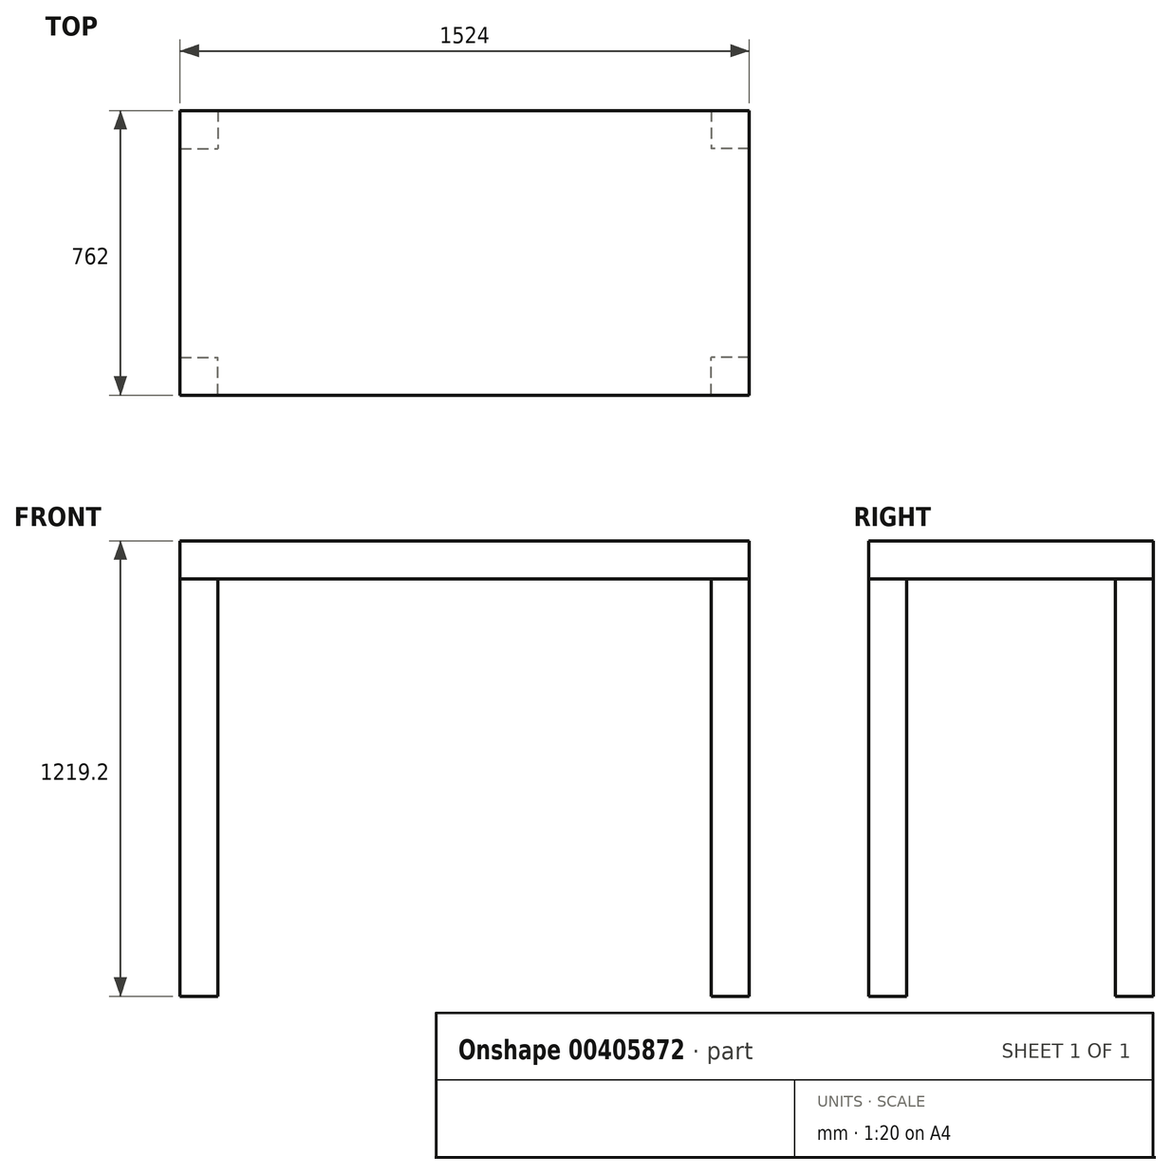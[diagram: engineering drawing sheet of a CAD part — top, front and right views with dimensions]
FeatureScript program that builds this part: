
annotation { "Feature Type Name" : "Feature", "Feature Type Description" : "" }
export const myFeature = defineFeature(function(context is Context, id is Id, definition is map)
    precondition{}
    {
        {
            assignVariable(context, id + "F0", {"name" : "TopThickness", "anyValue" : 101.6 * mm});
        }
        {
            assignVariable(context, id + "F1", {"name" : "Height", "anyValue" : 1219.2 * mm});
        }
        {
            var Q0;
            Q0=qCreatedBy(makeId("Top.planeOp"),FACE);
            var sketch = newSketch(context, id + "F2", { "sketchPlane" : qUnion([Q0])});
            skLineSegment(sketch, "E0", {"start": v(-762, 0) * mm, "end": v(762, 0) * mm, "construction": true});
            skLineSegment(sketch, "E1", {"start": v(0, 381) * mm, "end": v(0, -381) * mm, "construction": true});
            skLineSegment(sketch, "E2.bottom", {"start": v(-762, 381) * mm, "end": v(762, 381) * mm, "construction": true});
            skLineSegment(sketch, "E2.top", {"start": v(-762, -381) * mm, "end": v(762, -381) * mm, "construction": true});
            skLineSegment(sketch, "E2.left", {"start": v(-762, 381) * mm, "end": v(-762, -381) * mm, "construction": true});
            skLineSegment(sketch, "E2.right", {"start": v(762, 381) * mm, "end": v(762, -381) * mm, "construction": true});
            skSolve(sketch);
        }
        {
            var Q0;
            Q0=qCreatedBy(makeId("Top.planeOp"),FACE);
            cPlane(context, id + "F3", {"entities" : qUnion([Q0]), "cplaneType" : CPlaneType.OFFSET, "offset" : getVariable(context, 'TopThickness'), "width" : 152.4 * mm, "height" : 152.4 * mm});
        }
        {
            var Q0;
            Q0=qCreatedBy(makeId("Top.planeOp"),FACE);
            var sketch = newSketch(context, id + "F4", { "sketchPlane" : qUnion([Q0])});
            skPoint(sketch, "E3.0", {"position": v(-762, 381) * mm});
            skPoint(sketch, "E4.0", {"position": v(762, 381) * mm});
            skPoint(sketch, "E5.0", {"position": v(762, -381) * mm});
            skLineSegment(sketch, "E6.bottom", {"start": v(-762, 381) * mm, "end": v(-660.4, 381) * mm});
            skLineSegment(sketch, "E6.top", {"start": v(-762, 279.4) * mm, "end": v(-660.4, 279.4) * mm});
            skLineSegment(sketch, "E6.left", {"start": v(-762, 381) * mm, "end": v(-762, 279.4) * mm});
            skLineSegment(sketch, "E6.right", {"start": v(-660.4, 381) * mm, "end": v(-660.4, 279.4) * mm});
            skLineSegment(sketch, "E7.bottom", {"start": v(762, 381) * mm, "end": v(660.4, 381) * mm});
            skLineSegment(sketch, "E7.top", {"start": v(762, 279.4) * mm, "end": v(660.4, 279.4) * mm});
            skLineSegment(sketch, "E7.left", {"start": v(762, 381) * mm, "end": v(762, 279.4) * mm});
            skLineSegment(sketch, "E7.right", {"start": v(660.4, 381) * mm, "end": v(660.4, 279.4) * mm});
            skLineSegment(sketch, "E8.bottom", {"start": v(762, -381) * mm, "end": v(660.4, -381) * mm});
            skLineSegment(sketch, "E8.top", {"start": v(762, -279.4) * mm, "end": v(660.4, -279.4) * mm});
            skLineSegment(sketch, "E8.left", {"start": v(762, -381) * mm, "end": v(762, -279.4) * mm});
            skLineSegment(sketch, "E8.right", {"start": v(660.4, -381) * mm, "end": v(660.4, -279.4) * mm});
            skPoint(sketch, "E9.0", {"position": v(-762, -381) * mm});
            skLineSegment(sketch, "E10.bottom", {"start": v(-762, -381) * mm, "end": v(-660.4, -381) * mm});
            skLineSegment(sketch, "E10.top", {"start": v(-762, -279.4) * mm, "end": v(-660.4, -279.4) * mm});
            skLineSegment(sketch, "E10.left", {"start": v(-762, -381) * mm, "end": v(-762, -279.4) * mm});
            skLineSegment(sketch, "E10.right", {"start": v(-660.4, -381) * mm, "end": v(-660.4, -279.4) * mm});
            skSolve(sketch);
        }
        {
            var Q0;
            Q0 = qSketchRegion(id + "F4", true);
            extrude(context, id + "F5", {"entities" : qUnion([Q0]), "oppositeDirection" : true, "depth" : getVariable(context, 'Height') - getVariable(context, 'TopThickness')});
        }
        {
            var Q0;
            Q0=qCreatedBy(id+"F3.planeOp",FACE);
            var sketch = newSketch(context, id + "F6", { "sketchPlane" : qUnion([Q0])});
            skLineSegment(sketch, "E11.bottom", {"start": v(-762, -381) * mm, "end": v(762, -381) * mm});
            skLineSegment(sketch, "E11.top", {"start": v(-762, -330.2) * mm, "end": v(762, -330.2) * mm});
            skLineSegment(sketch, "E11.left", {"start": v(-762, -381) * mm, "end": v(-762, -330.2) * mm});
            skLineSegment(sketch, "E11.right", {"start": v(762, -381) * mm, "end": v(762, -330.2) * mm});
            skPoint(sketch, "E12.0", {"position": v(-762, -381) * mm});
            skLineSegment(sketch, "E13.0.1.0", {"start": v(-762, -279.4) * mm, "end": v(762, -279.4) * mm});
            skLineSegment(sketch, "E13.0.1.2", {"start": v(-762, -330.2) * mm, "end": v(-762, -279.4) * mm});
            skLineSegment(sketch, "E13.0.1.3", {"start": v(762, -330.2) * mm, "end": v(762, -279.4) * mm});
            skLineSegment(sketch, "E13.0.2.0", {"start": v(-762, -228.6) * mm, "end": v(762, -228.6) * mm});
            skLineSegment(sketch, "E13.0.2.1", {"start": v(-762, -279.4) * mm, "end": v(762, -279.4) * mm});
            skLineSegment(sketch, "E13.0.2.2", {"start": v(-762, -279.4) * mm, "end": v(-762, -228.6) * mm});
            skLineSegment(sketch, "E13.0.2.3", {"start": v(762, -279.4) * mm, "end": v(762, -228.6) * mm});
            skLineSegment(sketch, "E13.0.3.0", {"start": v(-762, -177.8) * mm, "end": v(762, -177.8) * mm});
            skLineSegment(sketch, "E13.0.3.1", {"start": v(-762, -228.6) * mm, "end": v(762, -228.6) * mm});
            skLineSegment(sketch, "E13.0.3.2", {"start": v(-762, -228.6) * mm, "end": v(-762, -177.8) * mm});
            skLineSegment(sketch, "E13.0.3.3", {"start": v(762, -228.6) * mm, "end": v(762, -177.8) * mm});
            skLineSegment(sketch, "E13.0.4.0", {"start": v(-762, -127) * mm, "end": v(762, -127) * mm});
            skLineSegment(sketch, "E13.0.4.1", {"start": v(-762, -177.8) * mm, "end": v(762, -177.8) * mm});
            skLineSegment(sketch, "E13.0.4.2", {"start": v(-762, -177.8) * mm, "end": v(-762, -127) * mm});
            skLineSegment(sketch, "E13.0.4.3", {"start": v(762, -177.8) * mm, "end": v(762, -127) * mm});
            skLineSegment(sketch, "E13.0.5.0", {"start": v(-762, -76.2) * mm, "end": v(762, -76.2) * mm});
            skLineSegment(sketch, "E13.0.5.1", {"start": v(-762, -127) * mm, "end": v(762, -127) * mm});
            skLineSegment(sketch, "E13.0.5.2", {"start": v(-762, -127) * mm, "end": v(-762, -76.2) * mm});
            skLineSegment(sketch, "E13.0.5.3", {"start": v(762, -127) * mm, "end": v(762, -76.2) * mm});
            skLineSegment(sketch, "E13.0.6.0", {"start": v(-762, -25.4) * mm, "end": v(762, -25.4) * mm});
            skLineSegment(sketch, "E13.0.6.1", {"start": v(-762, -76.2) * mm, "end": v(762, -76.2) * mm});
            skLineSegment(sketch, "E13.0.6.2", {"start": v(-762, -76.2) * mm, "end": v(-762, -25.4) * mm});
            skLineSegment(sketch, "E13.0.6.3", {"start": v(762, -76.2) * mm, "end": v(762, -25.4) * mm});
            skLineSegment(sketch, "E13.0.7.0", {"start": v(-762, 25.4) * mm, "end": v(762, 25.4) * mm});
            skLineSegment(sketch, "E13.0.7.1", {"start": v(-762, -25.4) * mm, "end": v(762, -25.4) * mm});
            skLineSegment(sketch, "E13.0.7.2", {"start": v(-762, -25.4) * mm, "end": v(-762, 25.4) * mm});
            skLineSegment(sketch, "E13.0.7.3", {"start": v(762, -25.4) * mm, "end": v(762, 25.4) * mm});
            skLineSegment(sketch, "E13.0.8.0", {"start": v(-762, 76.2) * mm, "end": v(762, 76.2) * mm});
            skLineSegment(sketch, "E13.0.8.1", {"start": v(-762, 25.4) * mm, "end": v(762, 25.4) * mm});
            skLineSegment(sketch, "E13.0.8.2", {"start": v(-762, 25.4) * mm, "end": v(-762, 76.2) * mm});
            skLineSegment(sketch, "E13.0.8.3", {"start": v(762, 25.4) * mm, "end": v(762, 76.2) * mm});
            skLineSegment(sketch, "E13.0.9.0", {"start": v(-762, 127) * mm, "end": v(762, 127) * mm});
            skLineSegment(sketch, "E13.0.9.1", {"start": v(-762, 76.2) * mm, "end": v(762, 76.2) * mm});
            skLineSegment(sketch, "E13.0.9.2", {"start": v(-762, 76.2) * mm, "end": v(-762, 127) * mm});
            skLineSegment(sketch, "E13.0.9.3", {"start": v(762, 76.2) * mm, "end": v(762, 127) * mm});
            skLineSegment(sketch, "E13.0.10.0", {"start": v(-762, 177.8) * mm, "end": v(762, 177.8) * mm});
            skLineSegment(sketch, "E13.0.10.1", {"start": v(-762, 127) * mm, "end": v(762, 127) * mm});
            skLineSegment(sketch, "E13.0.10.2", {"start": v(-762, 127) * mm, "end": v(-762, 177.8) * mm});
            skLineSegment(sketch, "E13.0.10.3", {"start": v(762, 127) * mm, "end": v(762, 177.8) * mm});
            skLineSegment(sketch, "E13.0.11.0", {"start": v(-762, 228.6) * mm, "end": v(762, 228.6) * mm});
            skLineSegment(sketch, "E13.0.11.1", {"start": v(-762, 177.8) * mm, "end": v(762, 177.8) * mm});
            skLineSegment(sketch, "E13.0.11.2", {"start": v(-762, 177.8) * mm, "end": v(-762, 228.6) * mm});
            skLineSegment(sketch, "E13.0.11.3", {"start": v(762, 177.8) * mm, "end": v(762, 228.6) * mm});
            skLineSegment(sketch, "E13.0.12.0", {"start": v(-762, 279.4) * mm, "end": v(762, 279.4) * mm});
            skLineSegment(sketch, "E13.0.12.1", {"start": v(-762, 228.6) * mm, "end": v(762, 228.6) * mm});
            skLineSegment(sketch, "E13.0.12.2", {"start": v(-762, 228.6) * mm, "end": v(-762, 279.4) * mm});
            skLineSegment(sketch, "E13.0.12.3", {"start": v(762, 228.6) * mm, "end": v(762, 279.4) * mm});
            skLineSegment(sketch, "E13.0.13.0", {"start": v(-762, 330.2) * mm, "end": v(762, 330.2) * mm});
            skLineSegment(sketch, "E13.0.13.1", {"start": v(-762, 279.4) * mm, "end": v(762, 279.4) * mm});
            skLineSegment(sketch, "E13.0.13.2", {"start": v(-762, 279.4) * mm, "end": v(-762, 330.2) * mm});
            skLineSegment(sketch, "E13.0.13.3", {"start": v(762, 279.4) * mm, "end": v(762, 330.2) * mm});
            skLineSegment(sketch, "E13.0.14.0", {"start": v(-762, 381) * mm, "end": v(762, 381) * mm});
            skLineSegment(sketch, "E13.0.14.1", {"start": v(-762, 330.2) * mm, "end": v(762, 330.2) * mm});
            skLineSegment(sketch, "E13.0.14.2", {"start": v(-762, 330.2) * mm, "end": v(-762, 381) * mm});
            skLineSegment(sketch, "E13.0.14.3", {"start": v(762, 330.2) * mm, "end": v(762, 381) * mm});
            skLineSegment(sketch, "E13.1.1.0", {"start": v(-762, -279.4) * mm, "end": v(762, -279.4) * mm});
            skLineSegment(sketch, "E13.1.1.2", {"start": v(-762, -330.2) * mm, "end": v(-762, -279.4) * mm});
            skLineSegment(sketch, "E13.1.1.3", {"start": v(762, -330.2) * mm, "end": v(762, -279.4) * mm});
            skLineSegment(sketch, "E13.1.2.0", {"start": v(-762, -228.6) * mm, "end": v(762, -228.6) * mm});
            skLineSegment(sketch, "E13.1.2.1", {"start": v(-762, -279.4) * mm, "end": v(762, -279.4) * mm});
            skLineSegment(sketch, "E13.1.2.2", {"start": v(-762, -279.4) * mm, "end": v(-762, -228.6) * mm});
            skLineSegment(sketch, "E13.1.2.3", {"start": v(762, -279.4) * mm, "end": v(762, -228.6) * mm});
            skLineSegment(sketch, "E13.1.3.0", {"start": v(-762, -177.8) * mm, "end": v(762, -177.8) * mm});
            skLineSegment(sketch, "E13.1.3.1", {"start": v(-762, -228.6) * mm, "end": v(762, -228.6) * mm});
            skLineSegment(sketch, "E13.1.3.2", {"start": v(-762, -228.6) * mm, "end": v(-762, -177.8) * mm});
            skLineSegment(sketch, "E13.1.3.3", {"start": v(762, -228.6) * mm, "end": v(762, -177.8) * mm});
            skLineSegment(sketch, "E13.1.4.0", {"start": v(-762, -127) * mm, "end": v(762, -127) * mm});
            skLineSegment(sketch, "E13.1.4.1", {"start": v(-762, -177.8) * mm, "end": v(762, -177.8) * mm});
            skLineSegment(sketch, "E13.1.4.2", {"start": v(-762, -177.8) * mm, "end": v(-762, -127) * mm});
            skLineSegment(sketch, "E13.1.4.3", {"start": v(762, -177.8) * mm, "end": v(762, -127) * mm});
            skLineSegment(sketch, "E13.1.5.0", {"start": v(-762, -76.2) * mm, "end": v(762, -76.2) * mm});
            skLineSegment(sketch, "E13.1.5.1", {"start": v(-762, -127) * mm, "end": v(762, -127) * mm});
            skLineSegment(sketch, "E13.1.5.2", {"start": v(-762, -127) * mm, "end": v(-762, -76.2) * mm});
            skLineSegment(sketch, "E13.1.5.3", {"start": v(762, -127) * mm, "end": v(762, -76.2) * mm});
            skLineSegment(sketch, "E13.1.6.0", {"start": v(-762, -25.4) * mm, "end": v(762, -25.4) * mm});
            skLineSegment(sketch, "E13.1.6.1", {"start": v(-762, -76.2) * mm, "end": v(762, -76.2) * mm});
            skLineSegment(sketch, "E13.1.6.2", {"start": v(-762, -76.2) * mm, "end": v(-762, -25.4) * mm});
            skLineSegment(sketch, "E13.1.6.3", {"start": v(762, -76.2) * mm, "end": v(762, -25.4) * mm});
            skLineSegment(sketch, "E13.1.7.0", {"start": v(-762, 25.4) * mm, "end": v(762, 25.4) * mm});
            skLineSegment(sketch, "E13.1.7.1", {"start": v(-762, -25.4) * mm, "end": v(762, -25.4) * mm});
            skLineSegment(sketch, "E13.1.7.2", {"start": v(-762, -25.4) * mm, "end": v(-762, 25.4) * mm});
            skLineSegment(sketch, "E13.1.7.3", {"start": v(762, -25.4) * mm, "end": v(762, 25.4) * mm});
            skLineSegment(sketch, "E13.1.8.0", {"start": v(-762, 76.2) * mm, "end": v(762, 76.2) * mm});
            skLineSegment(sketch, "E13.1.8.1", {"start": v(-762, 25.4) * mm, "end": v(762, 25.4) * mm});
            skLineSegment(sketch, "E13.1.8.2", {"start": v(-762, 25.4) * mm, "end": v(-762, 76.2) * mm});
            skLineSegment(sketch, "E13.1.8.3", {"start": v(762, 25.4) * mm, "end": v(762, 76.2) * mm});
            skLineSegment(sketch, "E13.1.9.0", {"start": v(-762, 127) * mm, "end": v(762, 127) * mm});
            skLineSegment(sketch, "E13.1.9.1", {"start": v(-762, 76.2) * mm, "end": v(762, 76.2) * mm});
            skLineSegment(sketch, "E13.1.9.2", {"start": v(-762, 76.2) * mm, "end": v(-762, 127) * mm});
            skLineSegment(sketch, "E13.1.9.3", {"start": v(762, 76.2) * mm, "end": v(762, 127) * mm});
            skLineSegment(sketch, "E13.1.10.0", {"start": v(-762, 177.8) * mm, "end": v(762, 177.8) * mm});
            skLineSegment(sketch, "E13.1.10.1", {"start": v(-762, 127) * mm, "end": v(762, 127) * mm});
            skLineSegment(sketch, "E13.1.10.2", {"start": v(-762, 127) * mm, "end": v(-762, 177.8) * mm});
            skLineSegment(sketch, "E13.1.10.3", {"start": v(762, 127) * mm, "end": v(762, 177.8) * mm});
            skLineSegment(sketch, "E13.1.11.0", {"start": v(-762, 228.6) * mm, "end": v(762, 228.6) * mm});
            skLineSegment(sketch, "E13.1.11.1", {"start": v(-762, 177.8) * mm, "end": v(762, 177.8) * mm});
            skLineSegment(sketch, "E13.1.11.2", {"start": v(-762, 177.8) * mm, "end": v(-762, 228.6) * mm});
            skLineSegment(sketch, "E13.1.11.3", {"start": v(762, 177.8) * mm, "end": v(762, 228.6) * mm});
            skLineSegment(sketch, "E13.1.12.0", {"start": v(-762, 279.4) * mm, "end": v(762, 279.4) * mm});
            skLineSegment(sketch, "E13.1.12.1", {"start": v(-762, 228.6) * mm, "end": v(762, 228.6) * mm});
            skLineSegment(sketch, "E13.1.12.2", {"start": v(-762, 228.6) * mm, "end": v(-762, 279.4) * mm});
            skLineSegment(sketch, "E13.1.12.3", {"start": v(762, 228.6) * mm, "end": v(762, 279.4) * mm});
            skLineSegment(sketch, "E13.1.13.0", {"start": v(-762, 330.2) * mm, "end": v(762, 330.2) * mm});
            skLineSegment(sketch, "E13.1.13.1", {"start": v(-762, 279.4) * mm, "end": v(762, 279.4) * mm});
            skLineSegment(sketch, "E13.1.13.2", {"start": v(-762, 279.4) * mm, "end": v(-762, 330.2) * mm});
            skLineSegment(sketch, "E13.1.13.3", {"start": v(762, 279.4) * mm, "end": v(762, 330.2) * mm});
            skLineSegment(sketch, "E13.1.14.0", {"start": v(-762, 381) * mm, "end": v(762, 381) * mm});
            skLineSegment(sketch, "E13.1.14.1", {"start": v(-762, 330.2) * mm, "end": v(762, 330.2) * mm});
            skLineSegment(sketch, "E13.1.14.2", {"start": v(-762, 330.2) * mm, "end": v(-762, 381) * mm});
            skLineSegment(sketch, "E13.1.14.3", {"start": v(762, 330.2) * mm, "end": v(762, 381) * mm});
            skLineSegment(sketch, "E13.2.1.0", {"start": v(-762, -279.4) * mm, "end": v(762, -279.4) * mm});
            skLineSegment(sketch, "E13.2.1.2", {"start": v(-762, -330.2) * mm, "end": v(-762, -279.4) * mm});
            skLineSegment(sketch, "E13.2.1.3", {"start": v(762, -330.2) * mm, "end": v(762, -279.4) * mm});
            skLineSegment(sketch, "E13.2.2.0", {"start": v(-762, -228.6) * mm, "end": v(762, -228.6) * mm});
            skLineSegment(sketch, "E13.2.2.1", {"start": v(-762, -279.4) * mm, "end": v(762, -279.4) * mm});
            skLineSegment(sketch, "E13.2.2.2", {"start": v(-762, -279.4) * mm, "end": v(-762, -228.6) * mm});
            skLineSegment(sketch, "E13.2.2.3", {"start": v(762, -279.4) * mm, "end": v(762, -228.6) * mm});
            skLineSegment(sketch, "E13.2.3.0", {"start": v(-762, -177.8) * mm, "end": v(762, -177.8) * mm});
            skLineSegment(sketch, "E13.2.3.1", {"start": v(-762, -228.6) * mm, "end": v(762, -228.6) * mm});
            skLineSegment(sketch, "E13.2.3.2", {"start": v(-762, -228.6) * mm, "end": v(-762, -177.8) * mm});
            skLineSegment(sketch, "E13.2.3.3", {"start": v(762, -228.6) * mm, "end": v(762, -177.8) * mm});
            skLineSegment(sketch, "E13.2.4.0", {"start": v(-762, -127) * mm, "end": v(762, -127) * mm});
            skLineSegment(sketch, "E13.2.4.1", {"start": v(-762, -177.8) * mm, "end": v(762, -177.8) * mm});
            skLineSegment(sketch, "E13.2.4.2", {"start": v(-762, -177.8) * mm, "end": v(-762, -127) * mm});
            skLineSegment(sketch, "E13.2.4.3", {"start": v(762, -177.8) * mm, "end": v(762, -127) * mm});
            skLineSegment(sketch, "E13.2.5.0", {"start": v(-762, -76.2) * mm, "end": v(762, -76.2) * mm});
            skLineSegment(sketch, "E13.2.5.1", {"start": v(-762, -127) * mm, "end": v(762, -127) * mm});
            skLineSegment(sketch, "E13.2.5.2", {"start": v(-762, -127) * mm, "end": v(-762, -76.2) * mm});
            skLineSegment(sketch, "E13.2.5.3", {"start": v(762, -127) * mm, "end": v(762, -76.2) * mm});
            skLineSegment(sketch, "E13.2.6.0", {"start": v(-762, -25.4) * mm, "end": v(762, -25.4) * mm});
            skLineSegment(sketch, "E13.2.6.1", {"start": v(-762, -76.2) * mm, "end": v(762, -76.2) * mm});
            skLineSegment(sketch, "E13.2.6.2", {"start": v(-762, -76.2) * mm, "end": v(-762, -25.4) * mm});
            skLineSegment(sketch, "E13.2.6.3", {"start": v(762, -76.2) * mm, "end": v(762, -25.4) * mm});
            skLineSegment(sketch, "E13.2.7.0", {"start": v(-762, 25.4) * mm, "end": v(762, 25.4) * mm});
            skLineSegment(sketch, "E13.2.7.1", {"start": v(-762, -25.4) * mm, "end": v(762, -25.4) * mm});
            skLineSegment(sketch, "E13.2.7.2", {"start": v(-762, -25.4) * mm, "end": v(-762, 25.4) * mm});
            skLineSegment(sketch, "E13.2.7.3", {"start": v(762, -25.4) * mm, "end": v(762, 25.4) * mm});
            skLineSegment(sketch, "E13.2.8.0", {"start": v(-762, 76.2) * mm, "end": v(762, 76.2) * mm});
            skLineSegment(sketch, "E13.2.8.1", {"start": v(-762, 25.4) * mm, "end": v(762, 25.4) * mm});
            skLineSegment(sketch, "E13.2.8.2", {"start": v(-762, 25.4) * mm, "end": v(-762, 76.2) * mm});
            skLineSegment(sketch, "E13.2.8.3", {"start": v(762, 25.4) * mm, "end": v(762, 76.2) * mm});
            skLineSegment(sketch, "E13.2.9.0", {"start": v(-762, 127) * mm, "end": v(762, 127) * mm});
            skLineSegment(sketch, "E13.2.9.1", {"start": v(-762, 76.2) * mm, "end": v(762, 76.2) * mm});
            skLineSegment(sketch, "E13.2.9.2", {"start": v(-762, 76.2) * mm, "end": v(-762, 127) * mm});
            skLineSegment(sketch, "E13.2.9.3", {"start": v(762, 76.2) * mm, "end": v(762, 127) * mm});
            skLineSegment(sketch, "E13.2.10.0", {"start": v(-762, 177.8) * mm, "end": v(762, 177.8) * mm});
            skLineSegment(sketch, "E13.2.10.1", {"start": v(-762, 127) * mm, "end": v(762, 127) * mm});
            skLineSegment(sketch, "E13.2.10.2", {"start": v(-762, 127) * mm, "end": v(-762, 177.8) * mm});
            skLineSegment(sketch, "E13.2.10.3", {"start": v(762, 127) * mm, "end": v(762, 177.8) * mm});
            skLineSegment(sketch, "E13.2.11.0", {"start": v(-762, 228.6) * mm, "end": v(762, 228.6) * mm});
            skLineSegment(sketch, "E13.2.11.1", {"start": v(-762, 177.8) * mm, "end": v(762, 177.8) * mm});
            skLineSegment(sketch, "E13.2.11.2", {"start": v(-762, 177.8) * mm, "end": v(-762, 228.6) * mm});
            skLineSegment(sketch, "E13.2.11.3", {"start": v(762, 177.8) * mm, "end": v(762, 228.6) * mm});
            skLineSegment(sketch, "E13.2.12.0", {"start": v(-762, 279.4) * mm, "end": v(762, 279.4) * mm});
            skLineSegment(sketch, "E13.2.12.1", {"start": v(-762, 228.6) * mm, "end": v(762, 228.6) * mm});
            skLineSegment(sketch, "E13.2.12.2", {"start": v(-762, 228.6) * mm, "end": v(-762, 279.4) * mm});
            skLineSegment(sketch, "E13.2.12.3", {"start": v(762, 228.6) * mm, "end": v(762, 279.4) * mm});
            skLineSegment(sketch, "E13.2.13.0", {"start": v(-762, 330.2) * mm, "end": v(762, 330.2) * mm});
            skLineSegment(sketch, "E13.2.13.1", {"start": v(-762, 279.4) * mm, "end": v(762, 279.4) * mm});
            skLineSegment(sketch, "E13.2.13.2", {"start": v(-762, 279.4) * mm, "end": v(-762, 330.2) * mm});
            skLineSegment(sketch, "E13.2.13.3", {"start": v(762, 279.4) * mm, "end": v(762, 330.2) * mm});
            skLineSegment(sketch, "E13.2.14.0", {"start": v(-762, 381) * mm, "end": v(762, 381) * mm});
            skLineSegment(sketch, "E13.2.14.1", {"start": v(-762, 330.2) * mm, "end": v(762, 330.2) * mm});
            skLineSegment(sketch, "E13.2.14.2", {"start": v(-762, 330.2) * mm, "end": v(-762, 381) * mm});
            skLineSegment(sketch, "E13.2.14.3", {"start": v(762, 330.2) * mm, "end": v(762, 381) * mm});
            skLineSegment(sketch, "E13.direction1", {"start": v(-762, -330.2) * mm, "end": v(-762, -330.2) * mm});
            skLineSegment(sketch, "E13.direction2", {"start": v(-762, -330.2) * mm, "end": v(-762, -279.4) * mm, "construction": true});
            skSolve(sketch);
        }
        {
            var Q0;
            Q0 = qSketchRegion(id + "F6", true);
            extrude(context, id + "F7", {"entities" : qUnion([Q0]), "oppositeDirection" : true, "depth" : getVariable(context, 'TopThickness')});
        }
    });
